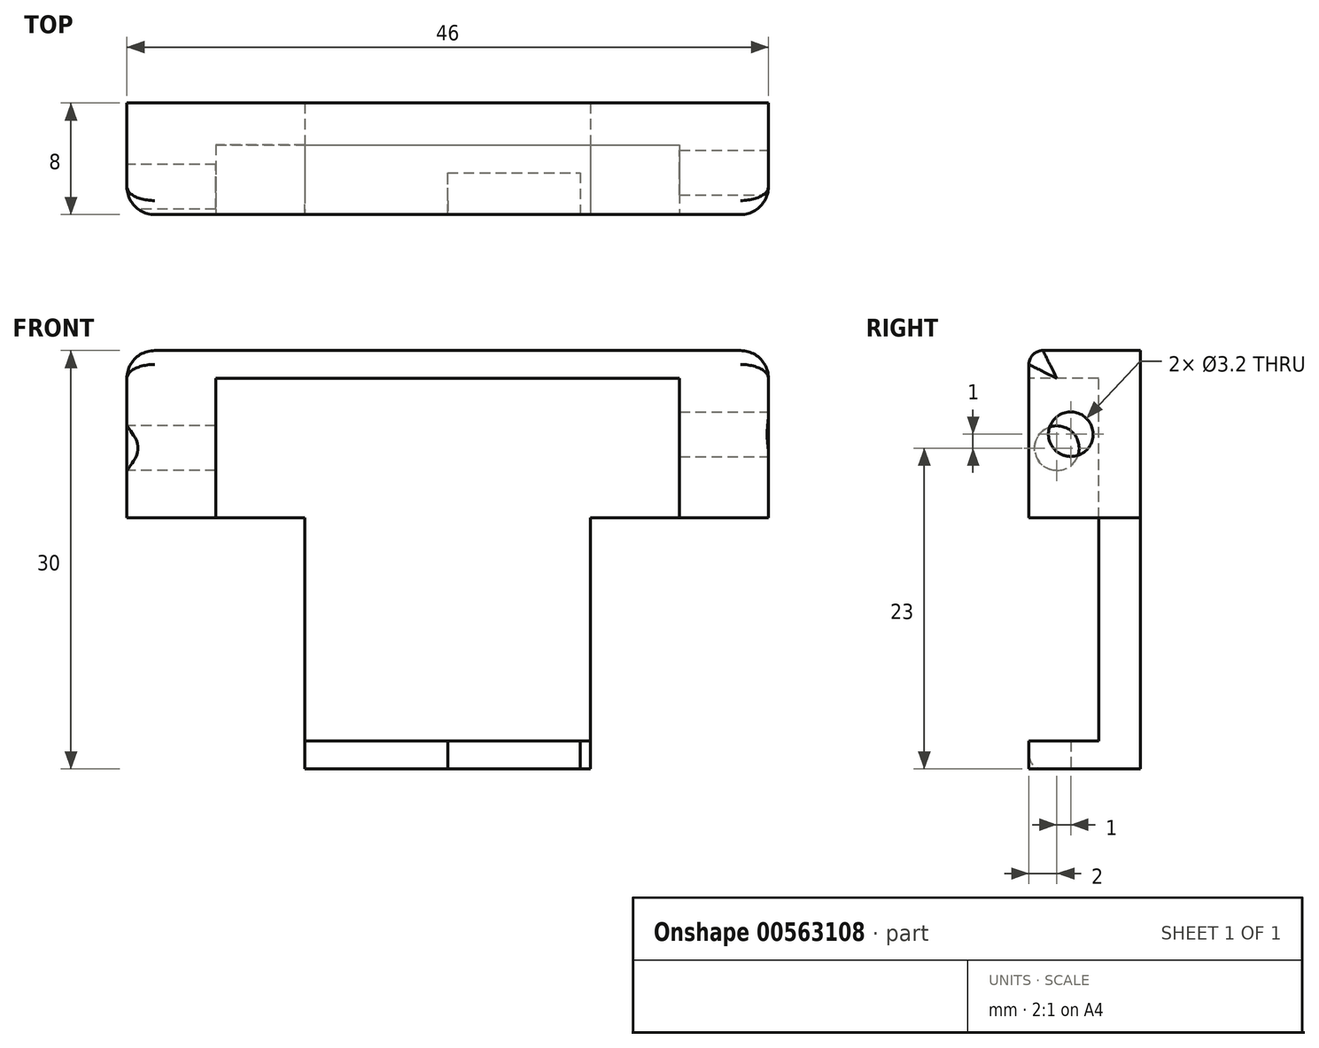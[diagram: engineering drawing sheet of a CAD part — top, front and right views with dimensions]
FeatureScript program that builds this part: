
annotation { "Feature Type Name" : "Feature", "Feature Type Description" : "" }
export const myFeature = defineFeature(function(context is Context, id is Id, definition is map)
    precondition{}
    {
        {
            var Q0;
            Q0=qCreatedBy(makeId("Front.planeOp"),FACE);
            var sketch = newSketch(context, id + "F0", { "sketchPlane" : qUnion([Q0])});
            skLineSegment(sketch, "E0", {"start": v(0, 0) * mm, "end": v(-23, 0) * mm});
            skLineSegment(sketch, "E1", {"start": v(0, 0) * mm, "end": v(23, 0) * mm});
            skLineSegment(sketch, "E2", {"start": v(23, 0) * mm, "end": v(23, 30) * mm});
            skLineSegment(sketch, "E3", {"start": v(23, 30) * mm, "end": v(-23, 30) * mm});
            skLineSegment(sketch, "E4", {"start": v(-23, 30) * mm, "end": v(-23, 0) * mm});
            skSolve(sketch);
        }
        {
            var Q0;
            Q0=makeQuery(id+"F0.imprint","IMPRINT",FACE,{"disambiguationData":[TD([[makeQuery(id+"F0.imprint","IMPRINT",EDGE,{"derivedFrom":sQuery(id+"F0.wireOp",EDGE,"E0")}),-1.0]])]});
            extrude(context, id + "F1", {"entities" : qUnion([Q0]), "depth" : 8 * mm, "offsetDistance" : 25 * mm});
        }
        {
            var Q0;
            Q0=makeQuery(id+"F1.opExtrude","CAP_FACE",FACE,{"disambiguationData":[OSD([sQuery(id+"F0.wireOp",EDGE,"E0"),sQuery(id+"F0.wireOp",EDGE,"E1"),sQuery(id+"F0.wireOp",EDGE,"E2"),sQuery(id+"F0.wireOp",EDGE,"E3"),sQuery(id+"F0.wireOp",EDGE,"E4")])],"isStart":false});
            var sketch = newSketch(context, id + "F2", { "sketchPlane" : qUnion([Q0])});
            skLineSegment(sketch, "E5", {"start": v(0, 0) * mm, "end": v(0, 2) * mm});
            skLineSegment(sketch, "E6", {"start": v(0, 2) * mm, "end": v(10.25, 2) * mm});
            skLineSegment(sketch, "E7", {"start": v(10.25, 2) * mm, "end": v(10.25, 18) * mm});
            skLineSegment(sketch, "E8", {"start": v(10.25, 18) * mm, "end": v(23, 18) * mm});
            skLineSegment(sketch, "E9", {"start": v(0, 2) * mm, "end": v(-10.25, 2) * mm});
            skLineSegment(sketch, "E10", {"start": v(-10.25, 2) * mm, "end": v(-10.25, 18) * mm});
            skLineSegment(sketch, "E11", {"start": v(-10.25, 18) * mm, "end": v(-23, 18) * mm});
            skLineSegment(sketch, "E12", {"start": v(-10.25, 2) * mm, "end": v(-10.25, 0) * mm});
            skLineSegment(sketch, "E13", {"start": v(10.25, 2) * mm, "end": v(10.25, 0) * mm});
            skSolve(sketch);
        }
        {
            var Q0;
            Q0=makeQuery(id+"F2.imprint","IMPRINT",FACE,{"disambiguationData":[TD([[makeQuery(id+"F2.imprint","IMPRINT",EDGE,{"derivedFrom":sQuery(id+"F2.wireOp",EDGE,"E10")}),1.0]])]});
            var Q1;
            Q1=makeQuery(id+"F2.imprint","IMPRINT",FACE,{"disambiguationData":[TD([[makeQuery(id+"F2.imprint","IMPRINT",EDGE,{"derivedFrom":sQuery(id+"F2.wireOp",EDGE,"E7")}),-1.0]])]});
            extrude(context, id + "F3", {"entities" : qUnion([Q0, Q1]), "operationType" : NewBodyOperationType.REMOVE, "oppositeDirection" : true, "depth" : 25 * mm, "offsetDistance" : 25 * mm});
        }
        {
            var Q0;
            Q0=makeQuery(id+"F1.opExtrude","CAP_FACE",FACE,{"disambiguationData":[OSD([sQuery(id+"F0.wireOp",EDGE,"E0"),sQuery(id+"F0.wireOp",EDGE,"E1"),sQuery(id+"F0.wireOp",EDGE,"E2"),sQuery(id+"F0.wireOp",EDGE,"E3"),sQuery(id+"F0.wireOp",EDGE,"E4")])],"isStart":false});
            var sketch = newSketch(context, id + "F4", { "sketchPlane" : qUnion([Q0])});
            skLineSegment(sketch, "E14", {"start": v(-10.25, 0) * mm, "end": v(-10.25, 2) * mm});
            skLineSegment(sketch, "E15", {"start": v(-10.25, 2) * mm, "end": v(10.25, 2) * mm});
            skLineSegment(sketch, "E16", {"start": v(16.62, 18) * mm, "end": v(16.62, 30) * mm});
            skLineSegment(sketch, "E17", {"start": v(-16.62, 18) * mm, "end": v(-16.62, 30) * mm});
            skLineSegment(sketch, "E18", {"start": v(-16.62, 30) * mm, "end": v(-16.62, 28) * mm});
            skLineSegment(sketch, "E19", {"start": v(-16.62, 28) * mm, "end": v(16.62, 28) * mm});
            skSolve(sketch);
        }
        {
            var Q0;
            {var subQ5=sQuery(id+"F4.wireOp",EDGE,"E15");Q0=makeQuery(id+"F4.imprint","IMPRINT",FACE,{"disambiguationData":[TD([[makeQuery(id+"F4.imprint","IMPRINT",EDGE,{"derivedFrom":subQ5}),1.0]])]});}
            extrude(context, id + "F5", {"entities" : qUnion([Q0]), "operationType" : NewBodyOperationType.REMOVE, "oppositeDirection" : true, "depth" : 5 * mm, "offsetDistance" : 25 * mm});
        }
        {
            var Q0;
            Q0=makeQuery(id+"F1.opExtrude","SWEPT_FACE",FACE,{"disambiguationData":[OSD([sQuery(id+"F0.wireOp",EDGE,"E0"),sQuery(id+"F0.wireOp",EDGE,"E1")])]});
            var sketch = newSketch(context, id + "F6", { "sketchPlane" : qUnion([Q0])});
            skLineSegment(sketch, "E20", {"start": v(9.5, 5) * mm, "end": v(9.5, 8) * mm});
            skLineSegment(sketch, "E21", {"start": v(9.5, 8) * mm, "end": v(0, 8) * mm});
            skLineSegment(sketch, "E22", {"start": v(0, 8) * mm, "end": v(0, 5) * mm});
            skLineSegment(sketch, "E23", {"start": v(0, 5) * mm, "end": v(9.5, 5) * mm});
            skSolve(sketch);
        }
        {
            var Q0;
            Q0=makeQuery(id+"F6.imprint","IMPRINT",FACE,{"disambiguationData":[TD([[makeQuery(id+"F6.imprint","IMPRINT",EDGE,{"derivedFrom":sQuery(id+"F6.wireOp",EDGE,"E20")}),1.0]])]});
            extrude(context, id + "F7", {"entities" : qUnion([Q0]), "operationType" : NewBodyOperationType.REMOVE, "oppositeDirection" : true, "depth" : 10 * mm, "offsetDistance" : 25 * mm});
        }
        {
            var Q0;
            Q0=makeQuery(id+"F1.opExtrude","SWEPT_FACE",FACE,{"disambiguationData":[OSD([sQuery(id+"F0.wireOp",EDGE,"E2")])]});
            var sketch = newSketch(context, id + "F8", { "sketchPlane" : qUnion([Q0])});
            skCircle(sketch, "E24", {"center": v(-5, 24) * mm, "radius": 1.6 * mm});
            skSolve(sketch);
        }
        {
            var Q0;
            Q0=makeQuery(id+"F8.imprint","IMPRINT",FACE,{"disambiguationData":[TD([[makeQuery(id+"F8.imprint","IMPRINT",EDGE,{"derivedFrom":sQuery(id+"F8.wireOp",EDGE,"E24")}),1.0]])]});
            extrude(context, id + "F9", {"entities" : qUnion([Q0]), "operationType" : NewBodyOperationType.REMOVE, "oppositeDirection" : true, "depth" : 10 * mm, "offsetDistance" : 25 * mm});
        }
        {
            var Q0;
            Q0=makeQuery(id+"F1.opExtrude","SWEPT_FACE",FACE,{"disambiguationData":[OSD([sQuery(id+"F0.wireOp",EDGE,"E4")])]});
            var sketch = newSketch(context, id + "F10", { "sketchPlane" : qUnion([Q0])});
            skCircle(sketch, "E25", {"center": v(6, 23) * mm, "radius": 1.6 * mm});
            skSolve(sketch);
        }
        {
            var Q0;
            Q0=makeQuery(id+"F10.imprint","IMPRINT",FACE,{"disambiguationData":[TD([[makeQuery(id+"F10.imprint","IMPRINT",EDGE,{"derivedFrom":sQuery(id+"F10.wireOp",EDGE,"E25")}),1.0]])]});
            extrude(context, id + "F11", {"entities" : qUnion([Q0]), "operationType" : NewBodyOperationType.REMOVE, "oppositeDirection" : true, "depth" : 10 * mm, "offsetDistance" : 25 * mm});
        }
        {
            var Q0;
            Q0=makeQuery(id+"F1.opExtrude","CAP_EDGE",EDGE,{"disambiguationData":[OSD([sQuery(id+"F0.wireOp",EDGE,"E3")])],"isStart":false});
            var Q1;
            Q1=makeQuery(id+"F3.boolean.opBoolean","COPY",EDGE,{"derivedFrom":makeQuery(id+"F3.opExtrude","CAP_EDGE",EDGE,{"disambiguationData":[OSD([sQuery(id+"F2.wireOp",EDGE,"E11")])],"isStart":true})});
            var Q2;
            Q2=makeQuery(id+"F3.boolean.opBoolean","COPY",EDGE,{"derivedFrom":makeQuery(id+"F3.opExtrude","CAP_EDGE",EDGE,{"disambiguationData":[OSD([sQuery(id+"F2.wireOp",EDGE,"E8")])],"isStart":true})});
            var Q3;
            {var subQ0=sQuery(id+"F0.wireOp",EDGE,"E1");var subQ1=sQuery(id+"F0.wireOp",EDGE,"E0");Q3=makeQuery(id+"F7.boolean.opBoolean","SPLIT",EDGE,{"disambiguationData":[TD([makeQuery(id+"F7.opExtrude","SWEPT_FACE",FACE,{"disambiguationData":[OSD([sQuery(id+"F6.wireOp",EDGE,"E22")])]})])],"derivedFrom":makeQuery(id+"F1.opExtrude","CAP_EDGE",EDGE,{"disambiguationData":[OSD([subQ1,subQ0])],"isStart":false})});}
            var Q4;
            Q4=makeQuery(id+"F5.boolean.opBoolean","COPY",EDGE,{"derivedFrom":makeQuery(id+"F5.opExtrude","CAP_EDGE",EDGE,{"disambiguationData":[OSD([sQuery(id+"F4.wireOp",EDGE,"E17")])],"isStart":true})});
            var Q5;
            Q5=makeQuery(id+"F5.boolean.opBoolean","COPY",EDGE,{"derivedFrom":makeQuery(id+"F5.opExtrude","CAP_EDGE",EDGE,{"disambiguationData":[OSD([sQuery(id+"F4.wireOp",EDGE,"E19")])],"isStart":true})});
            var Q6;
            Q6=makeQuery(id+"F5.boolean.opBoolean","COPY",EDGE,{"derivedFrom":makeQuery(id+"F5.opExtrude","CAP_EDGE",EDGE,{"disambiguationData":[OSD([sQuery(id+"F4.wireOp",EDGE,"E16")])],"isStart":true})});
            fillet(context, id + "F12", {"entities" : qUnion([Q0, Q1, Q2, Q3, Q4, Q5, Q6]), "radius" : 1 * mm, "tangentPropagation" : true, "allowEdgeOverflow" : false});
        }
        {
            var Q0;
            Q0=makeQuery(id+"F1.opExtrude","CAP_EDGE",EDGE,{"disambiguationData":[OSD([sQuery(id+"F0.wireOp",EDGE,"E4")])],"isStart":false});
            var Q1;
            Q1=makeQuery(id+"F1.opExtrude","CAP_EDGE",EDGE,{"disambiguationData":[OSD([sQuery(id+"F0.wireOp",EDGE,"E2")])],"isStart":false});
            fillet(context, id + "F13", {"entities" : qUnion([Q0, Q1]), "radius" : 2 * mm, "tangentPropagation" : true, "allowEdgeOverflow" : false});
        }
    });
